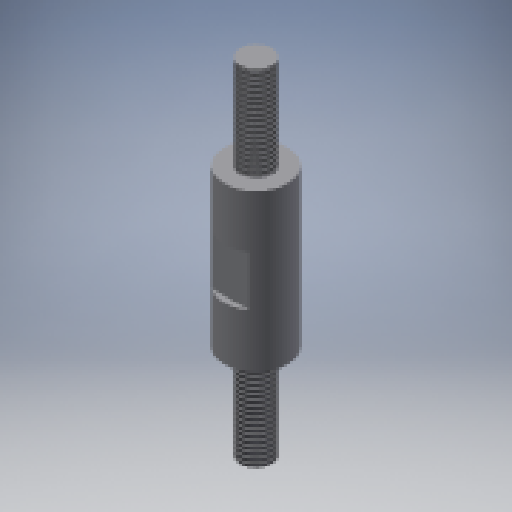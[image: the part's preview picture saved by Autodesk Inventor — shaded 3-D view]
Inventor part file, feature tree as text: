
AUTODESK INVENTOR PART (.ipt)
format: ipt  version: 2024.3 (Build 283343000, 343)  size: 302,080 bytes
history: native  units: mm
features: extrude x4, sketch x3, thread x1
ambient origin geometry x8: Origin, YZ Plane, XZ Plane, XY Plane, X Axis, Y Axis, Z Axis, Center Point
bodies: Volumenkörper1 (feature_tree)
feature tree (8):
  extrude  "Extrusion1"  Depth=25.0mm TaperAngle=0.0deg
  extrude  "Extrusion2"  Depth=15.0mm TaperAngle=0.0deg
  extrude  "Extrusion3"  Depth=8.0mm TaperAngle=0.0deg
  thread  "Gewinde1"  [1 undecoded]
  extrude  "Extrusion4"  Depth=8.0mm
  sketch  "Skizze2"  dims[d0=10.0mm d1=25.0mm d2=0.0mm]
  sketch  "Skizze3"  dims[d3=5.0mm d4=15.0mm d5=0.0mm]
  sketch  "Skizze4"  dims[d6=15.0mm d7=0.0mm d8=50.0mm d9=0.0mm d10=8.0mm d11=8.0mm d12=3.0mm d13=20.0mm d14=0.0mm]
note: 1 required parameter value undecoded (feature->parameter linkage not recoverable at this tier; creation-order binding heuristic only, values carry confidence <= 0.55)
